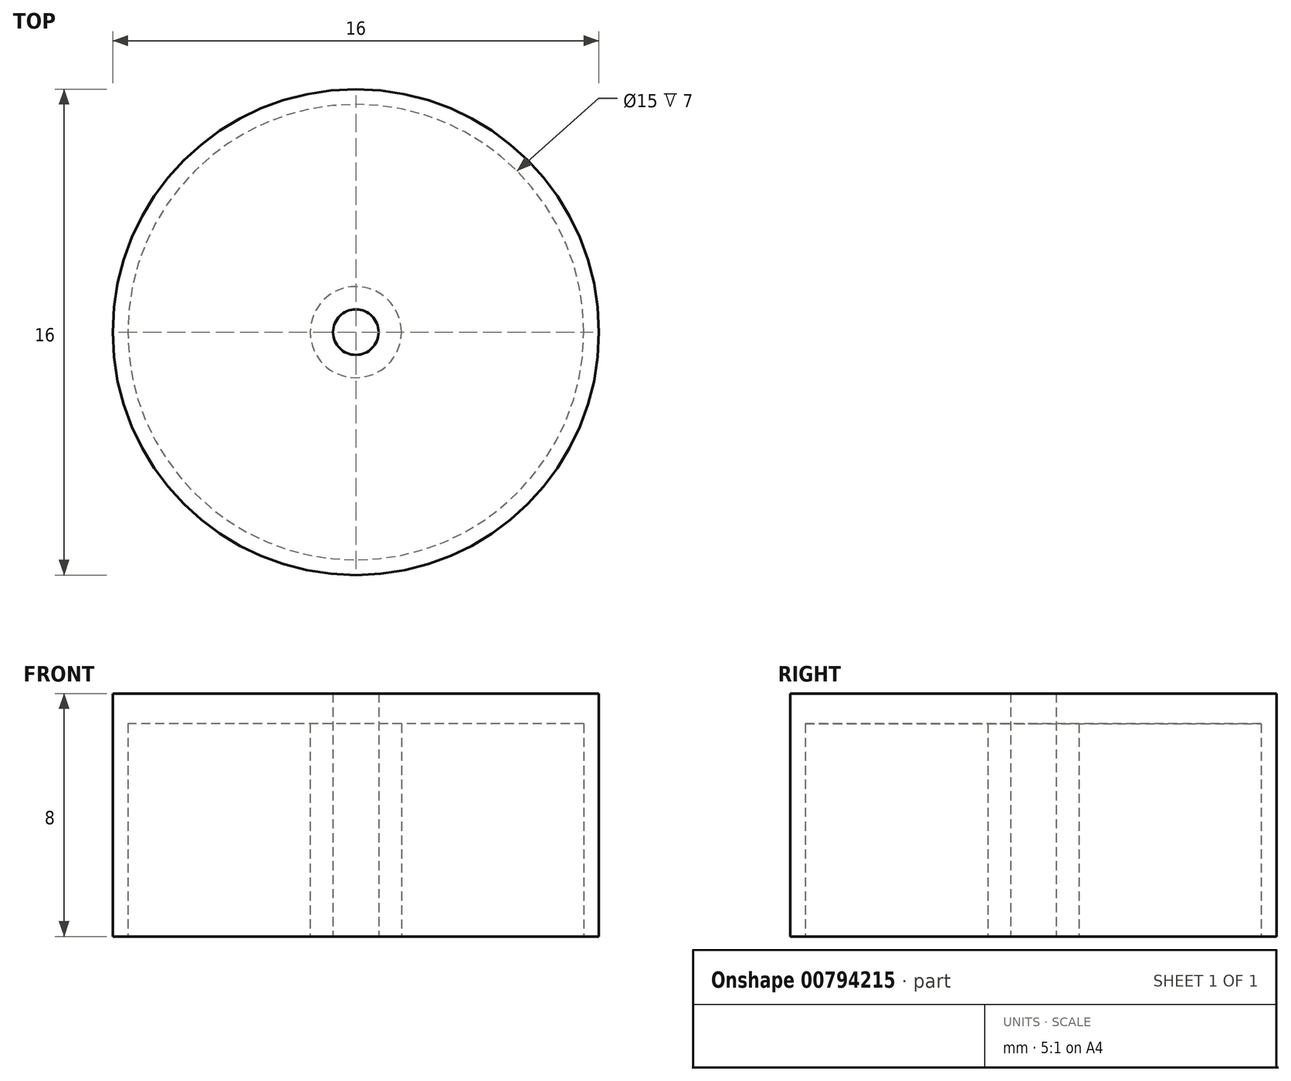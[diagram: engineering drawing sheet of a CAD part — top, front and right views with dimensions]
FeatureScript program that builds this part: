
annotation { "Feature Type Name" : "Feature", "Feature Type Description" : "" }
export const myFeature = defineFeature(function(context is Context, id is Id, definition is map)
    precondition{}
    {
        {
            var Q0;
            Q0=qCreatedBy(makeId("Top.planeOp"),FACE);
            var sketch = newSketch(context, id + "F0", { "sketchPlane" : qUnion([Q0])});
            skCircle(sketch, "E0", {"center": v(0, 0) * mm, "radius": 1.5 * mm});
            skCircle(sketch, "E1", {"center": v(0, 0) * mm, "radius": 7.5 * mm});
            skCircle(sketch, "E2", {"center": v(0, 0) * mm, "radius": 8 * mm});
            skCircle(sketch, "E3", {"center": v(0, 0) * mm, "radius": 0.75 * mm});
            skSolve(sketch);
        }
        {
            var Q0;
            Q0=makeQuery(id+"F0.imprint","IMPRINT",FACE,{"disambiguationData":[TD([[makeQuery(id+"F0.imprint","IMPRINT",EDGE,{"derivedFrom":sQuery(id+"F0.wireOp",EDGE,"E0")}),1.0]])]});
            var Q1;
            Q1=makeQuery(id+"F0.imprint","IMPRINT",FACE,{"disambiguationData":[TD([[makeQuery(id+"F0.imprint","IMPRINT",EDGE,{"derivedFrom":sQuery(id+"F0.wireOp",EDGE,"E1")}),-1.0]])]});
            extrude(context, id + "F1", {"entities" : qUnion([Q0, Q1]), "depth" : 7 * mm, "offsetDistance" : 25 * mm});
        }
        {
            var Q0;
            Q0=makeQuery(id+"F1.opExtrude","CAP_FACE",FACE,{"disambiguationData":[OSD([sQuery(id+"F0.wireOp",EDGE,"E0"),sQuery(id+"F0.wireOp",EDGE,"E3")])],"isStart":false});
            var sketch = newSketch(context, id + "F2", { "sketchPlane" : qUnion([Q0])});
            skCircle(sketch, "E4", {"center": v(0, 0) * mm, "radius": 8 * mm});
            skSolve(sketch);
        }
        {
            var Q0;
            Q0=makeQuery(id+"F2.imprint","IMPRINT",FACE,{"disambiguationData":[TD([[makeQuery(id+"F2.imprint","IMPRINT",EDGE,{"derivedFrom":sQuery(id+"F2.wireOp",EDGE,"E4")}),1.0]])]});
            var Q1;
            Q1=makeQuery(id+"F2.imprint","IMPRINT",FACE,{"disambiguationData":[TD([[makeQuery(id+"F2.imprint","IMPRINT",EDGE,{"derivedFrom":makeQuery(id+"F1.opExtrude","CAP_EDGE",EDGE,{"disambiguationData":[OSD([sQuery(id+"F0.wireOp",EDGE,"E0")])],"isStart":false})}),1.0]])]});
            extrude(context, id + "F3", {"entities" : qUnion([Q0, Q1]), "operationType" : NewBodyOperationType.ADD, "depth" : 1 * mm, "offsetDistance" : 25 * mm});
        }
    });
